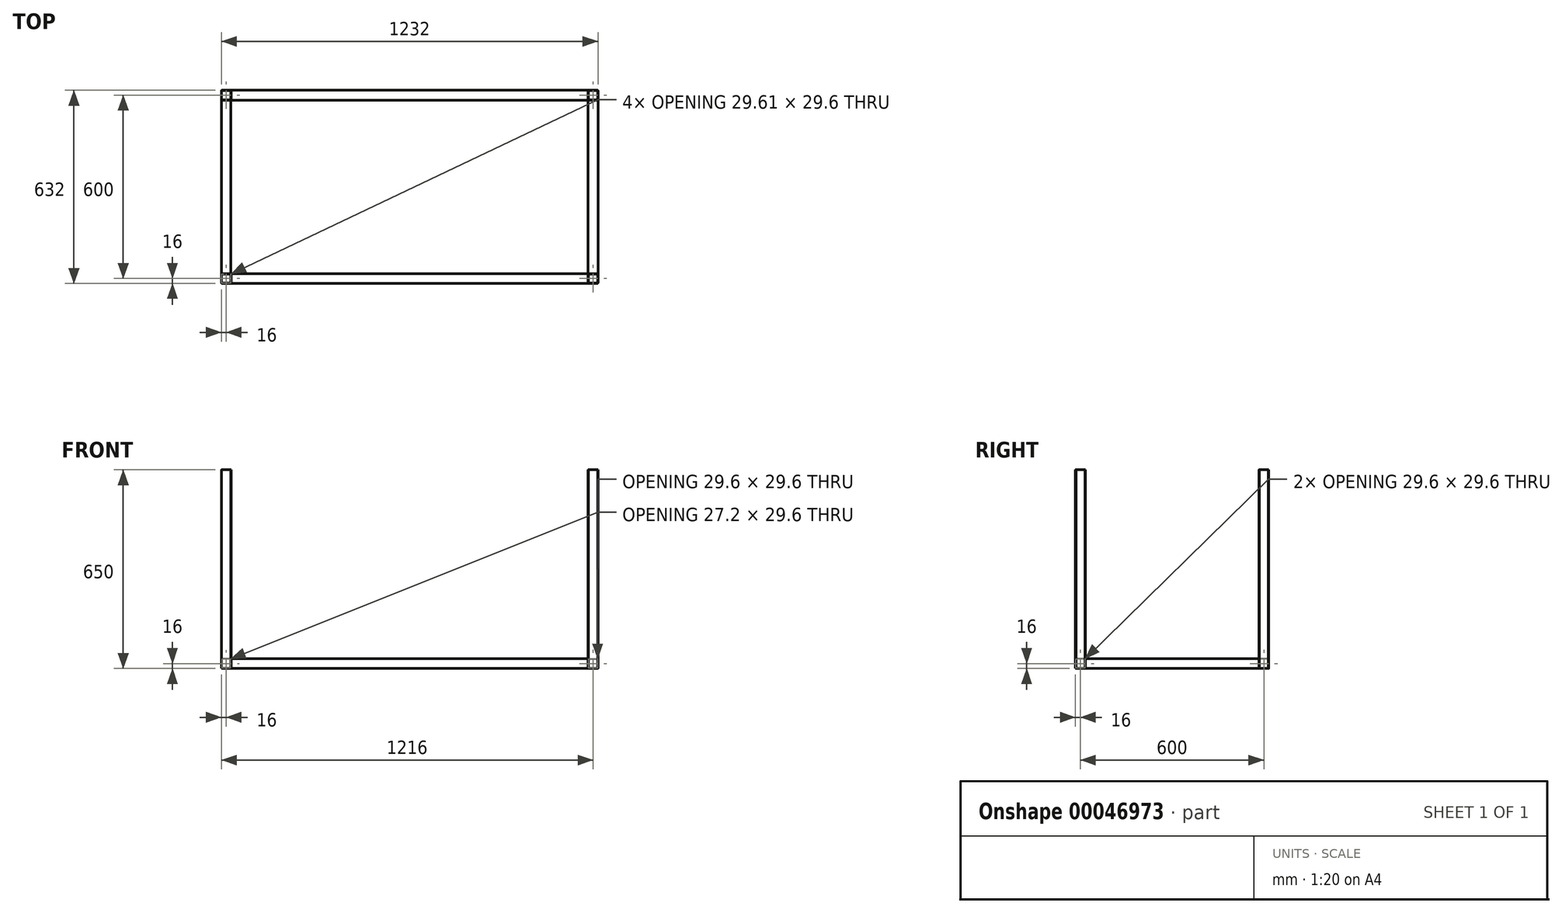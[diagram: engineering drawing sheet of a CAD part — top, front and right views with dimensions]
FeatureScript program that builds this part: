
annotation { "Feature Type Name" : "Feature", "Feature Type Description" : "" }
export const myFeature = defineFeature(function(context is Context, id is Id, definition is map)
    precondition{}
    {
        {
            var Q0;
            Q0=qCreatedBy(makeId("Top.planeOp"),FACE);
            var sketch = newSketch(context, id + "F0", { "sketchPlane" : qUnion([Q0])});
            skLineSegment(sketch, "E0.rect.bottom", {"start": v(-600, 300) * mm, "end": v(600, 300) * mm, "construction": true});
            skLineSegment(sketch, "E0.rect.top", {"start": v(-600, -300) * mm, "end": v(600, -300) * mm, "construction": true});
            skLineSegment(sketch, "E0.rect.left", {"start": v(-600, 300) * mm, "end": v(-600, -300) * mm, "construction": true});
            skLineSegment(sketch, "E0.rect.right", {"start": v(600, 300) * mm, "end": v(600, -300) * mm, "construction": true});
            skPoint(sketch, "E0.rect.middle", {"position": v(0, 0) * mm});
            skLineSegment(sketch, "E1.rect.bottom", {"start": v(-614.8, 316) * mm, "end": v(-585.2, 316) * mm});
            skLineSegment(sketch, "E1.rect.top", {"start": v(-614.8, 284) * mm, "end": v(-585.2, 284) * mm});
            skLineSegment(sketch, "E1.rect.left", {"start": v(-616, 314.7) * mm, "end": v(-616, 285.3) * mm});
            skLineSegment(sketch, "E1.rect.right", {"start": v(-584, 314.7) * mm, "end": v(-584, 285.3) * mm});
            skPoint(sketch, "E1.rect.middle", {"position": v(-600, 300) * mm});
            skLineSegment(sketch, "E2.rect.bottom", {"start": v(-613.9, 314.8) * mm, "end": v(-586.1, 314.8) * mm});
            skLineSegment(sketch, "E2.rect.top", {"start": v(-613.9, 285.2) * mm, "end": v(-586.1, 285.2) * mm});
            skLineSegment(sketch, "E2.rect.left", {"start": v(-614.8, 313.8) * mm, "end": v(-614.8, 286.2) * mm});
            skLineSegment(sketch, "E2.rect.right", {"start": v(-585.2, 313.8) * mm, "end": v(-585.2, 286.2) * mm});
            skArc(sketch, "E3", {"start": v(-614.8, 316) * mm, "mid": v(-615.63, 315.56) * mm, "end": v(-616, 314.7) * mm});
            skArc(sketch, "E4", {"start": v(-613.9, 314.8) * mm, "mid": v(-614.6, 314.34) * mm, "end": v(-614.8, 313.53) * mm});
            skPoint(sketch, "E5.orphan", {"position": v(-616, 316) * mm});
            skPoint(sketch, "E6.orphan", {"position": v(-614.8, 314.8) * mm});
            skLineSegment(sketch, "E7", {"start": v(-600, 300) * mm, "end": v(-600, 320.3) * mm, "construction": true});
            skArc(sketch, "E8.MirrorCS", {"start": v(-586.1, 314.8) * mm, "mid": v(-585.4, 314.34) * mm, "end": v(-585.2, 313.53) * mm});
            skArc(sketch, "E9.MirrorCS", {"start": v(-585.2, 316) * mm, "mid": v(-584.37, 315.56) * mm, "end": v(-584, 314.7) * mm});
            skPoint(sketch, "E10.MirrorP", {"position": v(-585.2, 314.8) * mm});
            skPoint(sketch, "E11.MirrorP", {"position": v(-584, 316) * mm});
            skPoint(sketch, "E12.MirrorP", {"position": v(-585.2, 285.2) * mm});
            skPoint(sketch, "E13.MirrorP", {"position": v(-584, 284) * mm});
            skArc(sketch, "E14.MirrorCS", {"start": v(-614.8, 284) * mm, "mid": v(-615.63, 284.44) * mm, "end": v(-616, 285.3) * mm});
            skPoint(sketch, "E15.MirrorP", {"position": v(-616, 284) * mm});
            skArc(sketch, "E16.MirrorCS", {"start": v(-585.2, 284) * mm, "mid": v(-584.37, 284.44) * mm, "end": v(-584, 285.3) * mm});
            skPoint(sketch, "E17.MirrorP", {"position": v(-614.8, 285.2) * mm});
            skArc(sketch, "E18.MirrorCS", {"start": v(-613.9, 285.2) * mm, "mid": v(-614.6, 285.66) * mm, "end": v(-614.8, 286.47) * mm});
            skArc(sketch, "E19.MirrorCS", {"start": v(-586.1, 285.2) * mm, "mid": v(-585.4, 285.66) * mm, "end": v(-585.2, 286.47) * mm});
            skArc(sketch, "E20.MirrorCS", {"start": v(586.1, 285.2) * mm, "mid": v(585.4, 285.66) * mm, "end": v(585.2, 286.47) * mm});
            skArc(sketch, "E21.MirrorCS", {"start": v(585.2, 284) * mm, "mid": v(584.37, 284.44) * mm, "end": v(584, 285.3) * mm});
            skArc(sketch, "E22.MirrorCS", {"start": v(613.9, 314.8) * mm, "mid": v(614.6, 314.34) * mm, "end": v(614.8, 313.53) * mm});
            skArc(sketch, "E23.MirrorCS", {"start": v(585.2, 316) * mm, "mid": v(584.37, 315.56) * mm, "end": v(584, 314.7) * mm});
            skArc(sketch, "E24.MirrorCS", {"start": v(586.1, 314.8) * mm, "mid": v(585.4, 314.34) * mm, "end": v(585.2, 313.53) * mm});
            skArc(sketch, "E25.MirrorCS", {"start": v(614.8, 316) * mm, "mid": v(615.63, 315.56) * mm, "end": v(616, 314.7) * mm});
            skPoint(sketch, "E26.MirrorP", {"position": v(584, 284) * mm});
            skPoint(sketch, "E27.MirrorP", {"position": v(585.2, 285.2) * mm});
            skLineSegment(sketch, "E28.MirrorCS", {"start": v(614.8, 316) * mm, "end": v(585.2, 316) * mm});
            skLineSegment(sketch, "E29.MirrorCS", {"start": v(600, 300) * mm, "end": v(600, 320.3) * mm});
            skPoint(sketch, "E30.MirrorP", {"position": v(616, 284) * mm});
            skPoint(sketch, "E31.MirrorP", {"position": v(614.8, 285.2) * mm});
            skPoint(sketch, "E32.MirrorP", {"position": v(585.2, 314.8) * mm});
            skLineSegment(sketch, "E33.MirrorCS", {"start": v(616, 314.7) * mm, "end": v(616, 285.3) * mm});
            skPoint(sketch, "E34.MirrorP", {"position": v(600, 300) * mm});
            skLineSegment(sketch, "E35.MirrorCS", {"start": v(613.9, 314.8) * mm, "end": v(586.1, 314.8) * mm});
            skLineSegment(sketch, "E36.MirrorCS", {"start": v(613.9, 285.2) * mm, "end": v(586.1, 285.2) * mm});
            skPoint(sketch, "E37.MirrorP", {"position": v(616, 316) * mm});
            skLineSegment(sketch, "E38.MirrorCS", {"start": v(614.8, 284) * mm, "end": v(585.2, 284) * mm});
            skPoint(sketch, "E39.MirrorP", {"position": v(584, 316) * mm});
            skPoint(sketch, "E40.MirrorP", {"position": v(614.8, 314.8) * mm});
            skLineSegment(sketch, "E41.MirrorCS", {"start": v(614.8, 313.8) * mm, "end": v(614.8, 286.2) * mm});
            skLineSegment(sketch, "E42.MirrorCS", {"start": v(584, 314.7) * mm, "end": v(584, 285.3) * mm});
            skLineSegment(sketch, "E43.MirrorCS", {"start": v(585.2, 313.8) * mm, "end": v(585.2, 286.2) * mm});
            skArc(sketch, "E44.MirrorCS", {"start": v(586.1, -285.2) * mm, "mid": v(585.4, -285.66) * mm, "end": v(585.2, -286.47) * mm});
            skArc(sketch, "E45.MirrorCS", {"start": v(-614.8, -284) * mm, "mid": v(-615.63, -284.44) * mm, "end": v(-616, -285.3) * mm});
            skLineSegment(sketch, "E46.MirrorCS", {"start": v(614.8, -284) * mm, "end": v(585.2, -284) * mm});
            skLineSegment(sketch, "E47.MirrorCS", {"start": v(-614.8, -284) * mm, "end": v(-585.2, -284) * mm});
            skLineSegment(sketch, "E48.MirrorCS", {"start": v(613.9, -285.2) * mm, "end": v(586.1, -285.2) * mm});
            skArc(sketch, "E49.MirrorCS", {"start": v(586.1, -314.8) * mm, "mid": v(585.4, -314.34) * mm, "end": v(585.2, -313.53) * mm});
            skLineSegment(sketch, "E50.MirrorCS", {"start": v(-613.9, -285.2) * mm, "end": v(-586.1, -285.2) * mm});
            skLineSegment(sketch, "E51.MirrorCS", {"start": v(584, -314.7) * mm, "end": v(584, -285.3) * mm});
            skArc(sketch, "E52.MirrorCS", {"start": v(614.8, -316) * mm, "mid": v(615.63, -315.56) * mm, "end": v(616, -314.7) * mm});
            skLineSegment(sketch, "E53.MirrorCS", {"start": v(614.8, -313.8) * mm, "end": v(614.8, -286.2) * mm});
            skLineSegment(sketch, "E54.MirrorCS", {"start": v(585.2, -313.8) * mm, "end": v(585.2, -286.2) * mm});
            skLineSegment(sketch, "E55.MirrorCS", {"start": v(616, -314.7) * mm, "end": v(616, -285.3) * mm});
            skArc(sketch, "E56.MirrorCS", {"start": v(613.9, -314.8) * mm, "mid": v(614.6, -314.34) * mm, "end": v(614.8, -313.53) * mm});
            skLineSegment(sketch, "E57.MirrorCS", {"start": v(600, -300) * mm, "end": v(600, -320.3) * mm});
            skArc(sketch, "E58.MirrorCS", {"start": v(585.2, -316) * mm, "mid": v(584.37, -315.56) * mm, "end": v(584, -314.7) * mm});
            skLineSegment(sketch, "E59.MirrorCS", {"start": v(-616, -314.7) * mm, "end": v(-616, -285.3) * mm});
            skLineSegment(sketch, "E60.MirrorCS", {"start": v(613.9, -314.8) * mm, "end": v(586.1, -314.8) * mm});
            skLineSegment(sketch, "E61.MirrorCS", {"start": v(614.8, -316) * mm, "end": v(585.2, -316) * mm});
            skLineSegment(sketch, "E62.MirrorCS", {"start": v(-614.8, -313.8) * mm, "end": v(-614.8, -286.2) * mm});
            skArc(sketch, "E63.MirrorCS", {"start": v(-614.8, -316) * mm, "mid": v(-615.63, -315.56) * mm, "end": v(-616, -314.7) * mm});
            skLineSegment(sketch, "E64.MirrorCS", {"start": v(-584, -314.7) * mm, "end": v(-584, -285.3) * mm});
            skArc(sketch, "E65.MirrorCS", {"start": v(-586.1, -314.8) * mm, "mid": v(-585.4, -314.34) * mm, "end": v(-585.2, -313.53) * mm});
            skLineSegment(sketch, "E66.MirrorCS", {"start": v(-585.2, -313.8) * mm, "end": v(-585.2, -286.2) * mm});
            skLineSegment(sketch, "E67.MirrorCS", {"start": v(-600, -300) * mm, "end": v(-600, -320.3) * mm});
            skPoint(sketch, "E68.MirrorP", {"position": v(584, -284) * mm});
            skPoint(sketch, "E69.MirrorP", {"position": v(-584, -284) * mm});
            skLineSegment(sketch, "E70.MirrorCS", {"start": v(-613.9, -314.8) * mm, "end": v(-586.1, -314.8) * mm});
            skLineSegment(sketch, "E71.MirrorCS", {"start": v(-614.8, -316) * mm, "end": v(-585.2, -316) * mm});
            skPoint(sketch, "E72.MirrorP", {"position": v(-614.8, -285.2) * mm});
            skPoint(sketch, "E73.MirrorP", {"position": v(-585.2, -285.2) * mm});
            skPoint(sketch, "E74.MirrorP", {"position": v(616, -284) * mm});
            skPoint(sketch, "E75.MirrorP", {"position": v(585.2, -285.2) * mm});
            skPoint(sketch, "E76.MirrorP", {"position": v(614.8, -285.2) * mm});
            skPoint(sketch, "E77.MirrorP", {"position": v(600, -300) * mm});
            skPoint(sketch, "E78.MirrorP", {"position": v(-600, -300) * mm});
            skPoint(sketch, "E79.MirrorP", {"position": v(-616, -284) * mm});
            skPoint(sketch, "E80.MirrorP", {"position": v(585.2, -314.8) * mm});
            skPoint(sketch, "E81.MirrorP", {"position": v(-584, -316) * mm});
            skPoint(sketch, "E82.MirrorP", {"position": v(584, -316) * mm});
            skPoint(sketch, "E83.MirrorP", {"position": v(614.8, -314.8) * mm});
            skPoint(sketch, "E84.MirrorP", {"position": v(-585.2, -314.8) * mm});
            skPoint(sketch, "E85.MirrorP", {"position": v(-614.8, -314.8) * mm});
            skPoint(sketch, "E86.MirrorP", {"position": v(616, -316) * mm});
            skPoint(sketch, "E87.MirrorP", {"position": v(-616, -316) * mm});
            skArc(sketch, "E88.MirrorCS", {"start": v(613.9, 285.2) * mm, "mid": v(614.6, 285.66) * mm, "end": v(614.8, 286.47) * mm});
            skArc(sketch, "E89.MirrorCS", {"start": v(585.2, -284) * mm, "mid": v(584.37, -284.44) * mm, "end": v(584, -285.3) * mm});
            skArc(sketch, "E90.MirrorCS", {"start": v(613.9, -285.2) * mm, "mid": v(614.6, -285.66) * mm, "end": v(614.8, -286.47) * mm});
            skArc(sketch, "E91.MirrorCS", {"start": v(-613.9, -285.2) * mm, "mid": v(-614.6, -285.66) * mm, "end": v(-614.8, -286.47) * mm});
            skArc(sketch, "E92.MirrorCS", {"start": v(-585.2, -284) * mm, "mid": v(-584.37, -284.44) * mm, "end": v(-584, -285.3) * mm});
            skArc(sketch, "E93.MirrorCS", {"start": v(-586.1, -285.2) * mm, "mid": v(-585.4, -285.66) * mm, "end": v(-585.2, -286.47) * mm});
            skLineSegment(sketch, "E94.MirrorCS", {"start": v(-600, -300) * mm, "end": v(600, -300) * mm});
            skArc(sketch, "E95.MirrorCS", {"start": v(614.8, 284) * mm, "mid": v(615.63, 284.44) * mm, "end": v(616, 285.3) * mm});
            skArc(sketch, "E96.MirrorCS", {"start": v(-585.2, -316) * mm, "mid": v(-584.37, -315.56) * mm, "end": v(-584, -314.7) * mm});
            skArc(sketch, "E97.MirrorCS", {"start": v(-613.9, -314.8) * mm, "mid": v(-614.6, -314.34) * mm, "end": v(-614.8, -313.53) * mm});
            skArc(sketch, "E98.MirrorCS", {"start": v(614.8, -284) * mm, "mid": v(615.63, -284.44) * mm, "end": v(616, -285.3) * mm});
            skSolve(sketch);
        }
        {
            var Q0;
            Q0=qSketchRegion(id+"F0",true);
            extrude(context, id + "F1", {"entities" : qUnion([Q0]), "depth" : 650 * mm});
        }
        {
            var Q0;
            Q0=qCreatedBy(makeId("Top.planeOp"),FACE);
            var sketch = newSketch(context, id + "F2", { "sketchPlane" : qUnion([Q0])});
            skLineSegment(sketch, "E99", {"start": v(584, 284) * mm, "end": v(584, 316) * mm});
            skLineSegment(sketch, "E100", {"start": v(584, 316) * mm, "end": v(-584, 316) * mm});
            skLineSegment(sketch, "E101", {"start": v(-584, 316) * mm, "end": v(-584, 284) * mm});
            skLineSegment(sketch, "E102", {"start": v(-584, 284) * mm, "end": v(584, 284) * mm});
            skLineSegment(sketch, "E103.MirrorCS", {"start": v(-584, -316) * mm, "end": v(-584, -284) * mm});
            skLineSegment(sketch, "E104.MirrorCS", {"start": v(584, -316) * mm, "end": v(-584, -316) * mm});
            skLineSegment(sketch, "E105.MirrorCS", {"start": v(584, -284) * mm, "end": v(584, -316) * mm});
            skLineSegment(sketch, "E106.MirrorCS", {"start": v(-584, -284) * mm, "end": v(584, -284) * mm});
            skSolve(sketch);
        }
        {
            var Q0;
            Q0=makeQuery(id+"F2.imprint","IMPRINT",FACE,{"disambiguationData":[TD([[makeQuery(id+"F2.imprint","IMPRINT",EDGE,{"derivedFrom":sQuery(id+"F2.wireOp",EDGE,"E99")}),1.0]])]});
            var Q1;
            Q1=makeQuery(id+"F2.imprint","IMPRINT",FACE,{"disambiguationData":[TD([[makeQuery(id+"F2.imprint","IMPRINT",EDGE,{"derivedFrom":sQuery(id+"F2.wireOp",EDGE,"E103.MirrorCS")}),-1.0]])]});
            extrude(context, id + "F3", {"entities" : qUnion([Q0, Q1]), "depth" : 32 * mm});
        }
        {
            var Q0;
            Q0=makeQuery(id+"F3.opExtrude","CAP_EDGE",EDGE,{"disambiguationData":[OSD([sQuery(id+"F2.wireOp",EDGE,"E100")])],"isStart":true});
            var Q1;
            Q1=makeQuery(id+"F3.opExtrude","CAP_EDGE",EDGE,{"disambiguationData":[OSD([sQuery(id+"F2.wireOp",EDGE,"E100")])],"isStart":false});
            var Q2;
            Q2=makeQuery(id+"F3.opExtrude","CAP_EDGE",EDGE,{"disambiguationData":[OSD([sQuery(id+"F2.wireOp",EDGE,"E102")])],"isStart":true});
            var Q3;
            Q3=makeQuery(id+"F3.opExtrude","CAP_EDGE",EDGE,{"disambiguationData":[OSD([sQuery(id+"F2.wireOp",EDGE,"E102")])],"isStart":false});
            var Q4;
            Q4=makeQuery(id+"F3.opExtrude","CAP_EDGE",EDGE,{"disambiguationData":[OSD([sQuery(id+"F2.wireOp",EDGE,"E104.MirrorCS")])],"isStart":true});
            var Q5;
            Q5=makeQuery(id+"F3.opExtrude","CAP_EDGE",EDGE,{"disambiguationData":[OSD([sQuery(id+"F2.wireOp",EDGE,"E106.MirrorCS")])],"isStart":true});
            var Q6;
            Q6=makeQuery(id+"F3.opExtrude","CAP_EDGE",EDGE,{"disambiguationData":[OSD([sQuery(id+"F2.wireOp",EDGE,"E104.MirrorCS")])],"isStart":false});
            var Q7;
            Q7=makeQuery(id+"F3.opExtrude","CAP_EDGE",EDGE,{"disambiguationData":[OSD([sQuery(id+"F2.wireOp",EDGE,"E106.MirrorCS")])],"isStart":false});
            fillet(context, id + "F4", {"entities" : qUnion([Q0, Q1, Q2, Q3, Q4, Q5, Q6, Q7]), "radius" : 1.5 * mm, "tangentPropagation" : true, "allowEdgeOverflow" : false});
        }
        {
            var Q0;
            Q0=makeQuery(id+"F3.opExtrude","SWEPT_FACE",FACE,{"disambiguationData":[OSD([sQuery(id+"F2.wireOp",EDGE,"E99")])]});
            var Q1;
            Q1=makeQuery(id+"F3.opExtrude","SWEPT_FACE",FACE,{"disambiguationData":[OSD([sQuery(id+"F2.wireOp",EDGE,"E101")])]});
            var Q2;
            Q2=makeQuery(id+"F3.opExtrude","SWEPT_FACE",FACE,{"disambiguationData":[OSD([sQuery(id+"F2.wireOp",EDGE,"E105.MirrorCS")])]});
            var Q3;
            Q3=makeQuery(id+"F3.opExtrude","SWEPT_FACE",FACE,{"disambiguationData":[OSD([sQuery(id+"F2.wireOp",EDGE,"E103.MirrorCS")])]});
            var Q4;
            Q4=makeQuery(id+"F3.opExtrude","SWEPT_BODY",BODY,{"disambiguationData":[OSD([sQuery(id+"F2.wireOp",EDGE,"E99"),sQuery(id+"F2.wireOp",EDGE,"E100"),sQuery(id+"F2.wireOp",EDGE,"E101"),sQuery(id+"F2.wireOp",EDGE,"E102")])]});
            shell(context, id + "F5", {"entities" : qUnion([Q0, Q1, Q2, Q3]), "parts" : qUnion([Q4]), "thickness" : 1.2 * mm});
        }
        {
            var Q0;
            Q0=makeQuery(id+"F1.opExtrude","SWEPT_FACE",FACE,{"disambiguationData":[OSD([sQuery(id+"F0.wireOp",EDGE,"E1.rect.top")])]});
            var sketch = newSketch(context, id + "F6", { "sketchPlane" : qUnion([Q0])});
            skLineSegment(sketch, "E107.bottom", {"start": v(-584, 0) * mm, "end": v(-616, 0) * mm});
            skLineSegment(sketch, "E107.top", {"start": v(-584, 32) * mm, "end": v(-616, 32) * mm});
            skLineSegment(sketch, "E107.left", {"start": v(-584, 0) * mm, "end": v(-584, 32) * mm});
            skLineSegment(sketch, "E107.right", {"start": v(-616, 0) * mm, "end": v(-616, 32) * mm});
            skPoint(sketch, "E108", {"position": v(-584, 0) * mm});
            skLineSegment(sketch, "E109.MirrorCS", {"start": v(584, 32) * mm, "end": v(616, 32) * mm});
            skLineSegment(sketch, "E110.MirrorCS", {"start": v(616, 0) * mm, "end": v(616, 32) * mm});
            skLineSegment(sketch, "E111.MirrorCS", {"start": v(584, 0) * mm, "end": v(584, 32) * mm});
            skLineSegment(sketch, "E112.MirrorCS", {"start": v(584, 0) * mm, "end": v(616, 0) * mm});
            skPoint(sketch, "E113.MirrorP", {"position": v(584, 0) * mm});
            skSolve(sketch);
        }
        {
            var Q0;
            {var subQ0=sQuery(id+"F0.wireOp",EDGE,"E1.rect.top");var subQ1=makeQuery(id+"F1.opExtrude","SWEPT_EDGE",EDGE,{"disambiguationData":[OSD([sQuery(id+"F0.wireOp",EDGE,"E16.MirrorCS"),subQ0])]});var subQ4=sQuery(id+"F6.wireOp",EDGE,"E107.bottom");var subQ5=makeQuery(id+"F6.imprint","INTERSECT",VERTEX,{"derivedFrom":[subQ1,subQ4]});var subQ6=makeQuery(id+"F1.opExtrude","SWEPT_EDGE",EDGE,{"disambiguationData":[OSD([sQuery(id+"F0.wireOp",EDGE,"E14.MirrorCS"),subQ0])]});var subQ8=makeQuery(id+"F6.imprint","INTERSECT",VERTEX,{"derivedFrom":[subQ6,subQ4]});Q0=makeQuery(id+"F6.imprint","IMPRINT",FACE,{"disambiguationData":[TD([[makeQuery(id+"F6.imprint","IMPRINT",EDGE,{"disambiguationData":[TD([[subQ8,-1.0],[subQ5,1.0]])],"derivedFrom":subQ4}),1.0]])]});}
            var Q1;
            Q1=makeQuery(id+"F6.imprint","IMPRINT",FACE,{"disambiguationData":[TD([[makeQuery(id+"F6.imprint","IMPRINT",EDGE,{"derivedFrom":sQuery(id+"F6.wireOp",EDGE,"E109.MirrorCS")}),-1.0]])]});
            extrude(context, id + "F7", {"entities" : qUnion([Q0, Q1]), "depth" : 568 * mm});
        }
        {
            var Q0;
            Q0=makeQuery(id+"F7.opExtrude","SWEPT_EDGE",EDGE,{"disambiguationData":[OSD([sQuery(id+"F0.wireOp",EDGE,"E14.MirrorCS"),sQuery(id+"F0.wireOp",EDGE,"E1.rect.top"),sQuery(id+"F6.wireOp",EDGE,"E107.top")])]});
            var Q1;
            Q1=makeQuery(id+"F7.opExtrude","SWEPT_EDGE",EDGE,{"disambiguationData":[OSD([sQuery(id+"F0.wireOp",EDGE,"E16.MirrorCS"),sQuery(id+"F0.wireOp",EDGE,"E1.rect.top"),sQuery(id+"F6.wireOp",EDGE,"E107.top")])]});
            var Q2;
            Q2=makeQuery(id+"F7.opExtrude","SWEPT_EDGE",EDGE,{"disambiguationData":[OSD([sQuery(id+"F0.wireOp",EDGE,"E16.MirrorCS"),sQuery(id+"F0.wireOp",EDGE,"E1.rect.top"),sQuery(id+"F6.wireOp",EDGE,"E107.bottom")])]});
            var Q3;
            Q3=makeQuery(id+"F7.opExtrude","SWEPT_EDGE",EDGE,{"disambiguationData":[OSD([sQuery(id+"F0.wireOp",EDGE,"E14.MirrorCS"),sQuery(id+"F0.wireOp",EDGE,"E1.rect.top"),sQuery(id+"F6.wireOp",EDGE,"E107.bottom")])]});
            var Q4;
            Q4=makeQuery(id+"F7.opExtrude","SWEPT_EDGE",EDGE,{"disambiguationData":[OSD([sQuery(id+"F6.wireOp",EDGE,"E109.MirrorCS"),sQuery(id+"F6.wireOp",EDGE,"E111.MirrorCS")])]});
            var Q5;
            Q5=makeQuery(id+"F7.opExtrude","SWEPT_EDGE",EDGE,{"disambiguationData":[OSD([sQuery(id+"F6.wireOp",EDGE,"E111.MirrorCS"),sQuery(id+"F6.wireOp",EDGE,"E112.MirrorCS")])]});
            var Q6;
            Q6=makeQuery(id+"F7.opExtrude","SWEPT_EDGE",EDGE,{"disambiguationData":[OSD([sQuery(id+"F6.wireOp",EDGE,"E109.MirrorCS"),sQuery(id+"F6.wireOp",EDGE,"E110.MirrorCS")])]});
            var Q7;
            Q7=makeQuery(id+"F7.opExtrude","SWEPT_EDGE",EDGE,{"disambiguationData":[OSD([sQuery(id+"F6.wireOp",EDGE,"E110.MirrorCS"),sQuery(id+"F6.wireOp",EDGE,"E112.MirrorCS")])]});
            fillet(context, id + "F8", {"entities" : qUnion([Q0, Q1, Q2, Q3, Q4, Q5, Q6, Q7]), "radius" : 1.5 * mm, "tangentPropagation" : true, "allowEdgeOverflow" : false});
        }
        {
            var Q0;
            Q0=makeQuery(id+"F7.opExtrude","CAP_FACE",FACE,{"disambiguationData":[OSD([sQuery(id+"F0.wireOp",EDGE,"E14.MirrorCS"),sQuery(id+"F0.wireOp",EDGE,"E16.MirrorCS"),sQuery(id+"F0.wireOp",EDGE,"E1.rect.top"),sQuery(id+"F6.wireOp",EDGE,"E107.bottom"),sQuery(id+"F6.wireOp",EDGE,"E107.top")])],"isStart":false});
            var Q1;
            Q1=makeQuery(id+"F7.opExtrude","CAP_FACE",FACE,{"disambiguationData":[OSD([sQuery(id+"F0.wireOp",EDGE,"E14.MirrorCS"),sQuery(id+"F0.wireOp",EDGE,"E16.MirrorCS"),sQuery(id+"F0.wireOp",EDGE,"E1.rect.top"),sQuery(id+"F6.wireOp",EDGE,"E107.bottom"),sQuery(id+"F6.wireOp",EDGE,"E107.top")])],"isStart":true});
            var Q2;
            Q2=makeQuery(id+"F7.opExtrude","CAP_FACE",FACE,{"disambiguationData":[OSD([sQuery(id+"F6.wireOp",EDGE,"E109.MirrorCS"),sQuery(id+"F6.wireOp",EDGE,"E110.MirrorCS"),sQuery(id+"F6.wireOp",EDGE,"E111.MirrorCS"),sQuery(id+"F6.wireOp",EDGE,"E112.MirrorCS")])],"isStart":true});
            var Q3;
            Q3=makeQuery(id+"F7.opExtrude","CAP_FACE",FACE,{"disambiguationData":[OSD([sQuery(id+"F6.wireOp",EDGE,"E109.MirrorCS"),sQuery(id+"F6.wireOp",EDGE,"E110.MirrorCS"),sQuery(id+"F6.wireOp",EDGE,"E111.MirrorCS"),sQuery(id+"F6.wireOp",EDGE,"E112.MirrorCS")])],"isStart":false});
            shell(context, id + "F9", {"entities" : qUnion([Q0, Q1, Q2, Q3]), "thickness" : 1.2 * mm});
        }
    });
